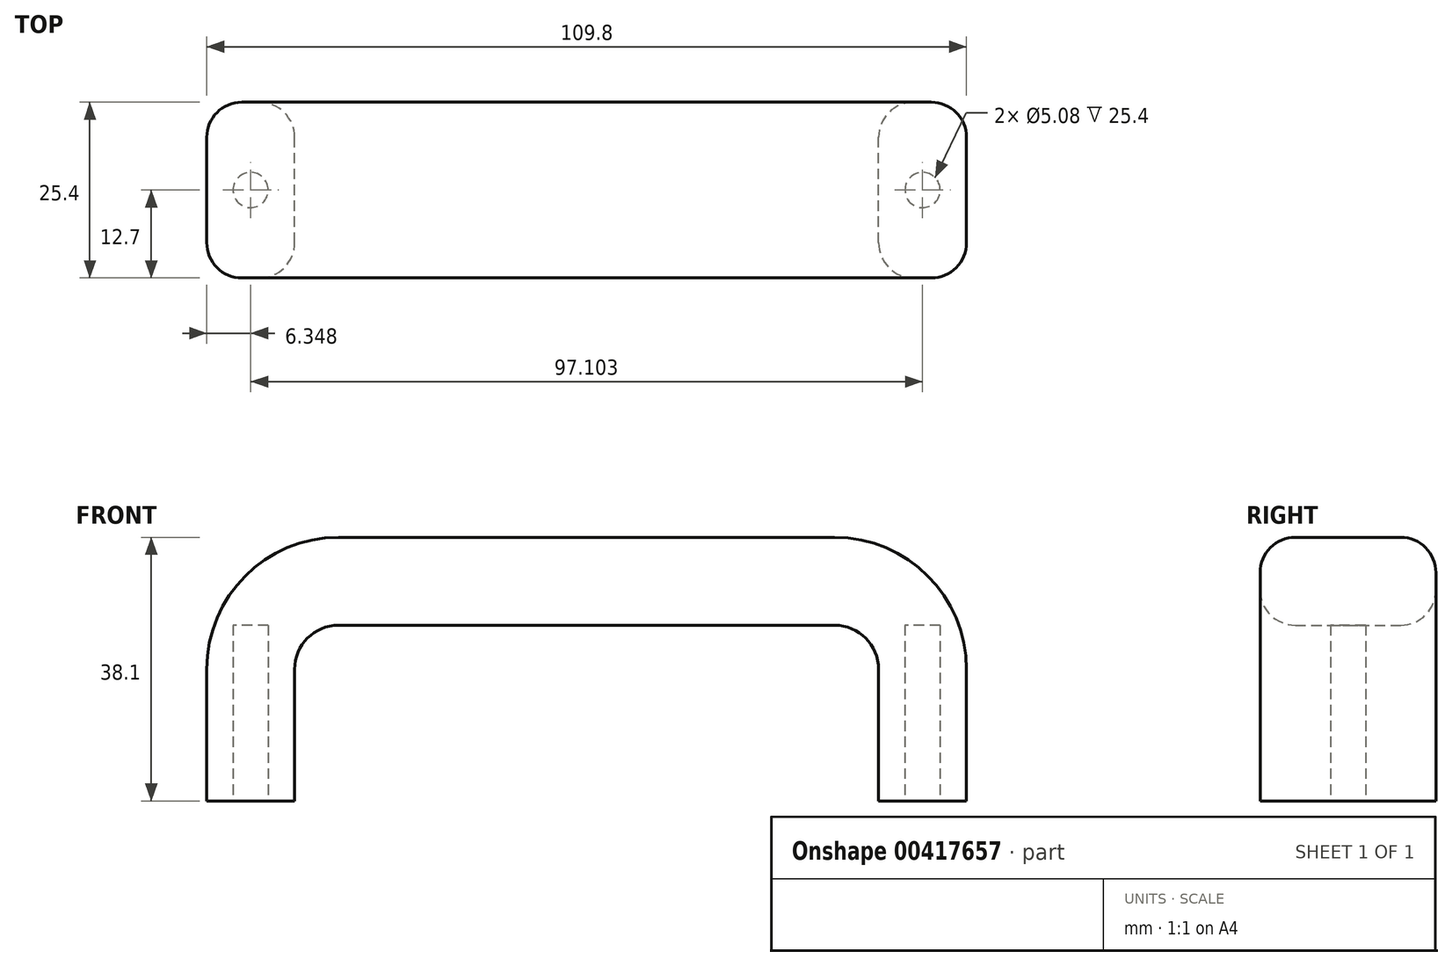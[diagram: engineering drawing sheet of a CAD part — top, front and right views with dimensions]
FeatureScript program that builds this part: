
annotation { "Feature Type Name" : "Feature", "Feature Type Description" : "" }
export const myFeature = defineFeature(function(context is Context, id is Id, definition is map)
    precondition{}
    {
        {
            var Q0;
            Q0=qCreatedBy(makeId("Front.planeOp"),FACE);
            var sketch = newSketch(context, id + "F0", { "sketchPlane" : qUnion([Q0])});
            skLineSegment(sketch, "E0.bottom", {"start": v(35.85, 38.1) * mm, "end": v(-35.85, 38.1) * mm});
            skLineSegment(sketch, "E0.left", {"start": v(54.9, 19.05) * mm, "end": v(54.9, 0) * mm});
            skLineSegment(sketch, "E0.right", {"start": v(-54.9, 19.05) * mm, "end": v(-54.9, 0) * mm});
            skPoint(sketch, "E0.middle", {"position": v(0, 0) * mm});
            skLineSegment(sketch, "E1", {"start": v(-54.9, 0) * mm, "end": v(-42.2, 0) * mm});
            skPoint(sketch, "E0.top.end.orphan", {"position": v(-54.9, -38.1) * mm});
            skPoint(sketch, "E2.orphan", {"position": v(54.9, -38.1) * mm});
            skLineSegment(sketch, "E3", {"start": v(-42.2, 0) * mm, "end": v(-42.2, 19.05) * mm});
            skLineSegment(sketch, "E4", {"start": v(-35.85, 25.4) * mm, "end": v(35.85, 25.4) * mm});
            skLineSegment(sketch, "E5", {"start": v(42.2, 19.05) * mm, "end": v(42.2, 0) * mm});
            skLineSegment(sketch, "E6.trimOffspring", {"start": v(42.2, 0) * mm, "end": v(54.9, 0) * mm});
            skPoint(sketch, "E7.visualSharp", {"position": v(-54.9, 38.1) * mm});
            skArc(sketch, "E7.filletArc", {"start": v(-35.85, 38.1) * mm, "mid": v(-49.32, 32.52) * mm, "end": v(-54.9, 19.05) * mm});
            skPoint(sketch, "E8.visualSharp", {"position": v(54.9, 38.1) * mm});
            skArc(sketch, "E8.filletArc", {"start": v(54.9, 19.05) * mm, "mid": v(49.32, 32.52) * mm, "end": v(35.85, 38.1) * mm});
            skPoint(sketch, "E9.visualSharp", {"position": v(-42.2, 25.4) * mm});
            skArc(sketch, "E9.filletArc", {"start": v(-35.85, 25.4) * mm, "mid": v(-40.34, 23.54) * mm, "end": v(-42.2, 19.05) * mm});
            skPoint(sketch, "E10.visualSharp", {"position": v(42.2, 25.4) * mm});
            skArc(sketch, "E10.filletArc", {"start": v(42.2, 19.05) * mm, "mid": v(40.34, 23.54) * mm, "end": v(35.85, 25.4) * mm});
            skSolve(sketch);
        }
        {
            var Q0;
            Q0 = qSketchRegion(id + "F0", true);
            extrude(context, id + "F1", {"entities" : qUnion([Q0]), "depth" : 25.4 * mm});
        }
        {
            var Q0;
            Q0=makeQuery(id+"F1.opExtrude","CAP_EDGE",EDGE,{"disambiguationData":[OSD([sQuery(id+"F0.wireOp",EDGE,"E0.bottom")])],"isStart":false});
            var Q1;
            Q1=makeQuery(id+"F1.opExtrude","CAP_EDGE",EDGE,{"disambiguationData":[OSD([sQuery(id+"F0.wireOp",EDGE,"E0.bottom")])],"isStart":true});
            var Q2;
            Q2=makeQuery(id+"F1.opExtrude","CAP_EDGE",EDGE,{"disambiguationData":[OSD([sQuery(id+"F0.wireOp",EDGE,"E4")])],"isStart":false});
            var Q3;
            Q3=makeQuery(id+"F1.opExtrude","CAP_EDGE",EDGE,{"disambiguationData":[OSD([sQuery(id+"F0.wireOp",EDGE,"E4")])],"isStart":true});
            fillet(context, id + "F2", {"entities" : qUnion([Q0, Q1, Q2, Q3]), "radius" : 5.08 * mm, "tangentPropagation" : true, "allowEdgeOverflow" : false});
        }
        {
            var Q0;
            Q0=qCreatedBy(makeId("Top.planeOp"),FACE);
            var sketch = newSketch(context, id + "F3", { "sketchPlane" : qUnion([Q0])});
            skCircle(sketch, "E11", {"center": v(-48.55, -12.7) * mm, "radius": 2.54 * mm});
            skCircle(sketch, "E12", {"center": v(48.55, -12.7) * mm, "radius": 2.54 * mm});
            skLineSegment(sketch, "E13", {"start": v(-54.95, -12.7) * mm, "end": v(54.8, -12.7) * mm, "construction": true});
            skSolve(sketch);
        }
        {
            var Q0;
            Q0 = qSketchRegion(id + "F3", true);
            extrude(context, id + "F4", {"entities" : qUnion([Q0]), "operationType" : NewBodyOperationType.REMOVE, "depth" : 25.4 * mm});
        }
    });
